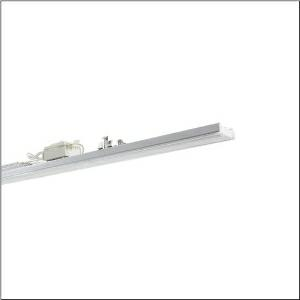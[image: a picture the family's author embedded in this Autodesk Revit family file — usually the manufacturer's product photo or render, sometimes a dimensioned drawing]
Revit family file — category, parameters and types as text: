
# Revit family: licross_21_recessed_ho_52tl18de47xm
name_source: partatom
category: Lighting Fixtures
units: mm (PartAtom-declared; Revit-internal decimal feet)

## family parameters
Cut with Voids When Loaded = No
Host = Face
Light Source = No
Part Type = Normal
Room Calculation Point = No
Round Connector Dimension = Use Diameter
Shared = No

## types (1)
- --- (1 x LED, 7420 lm, 44.1 W, 4000K)
    Apparent Load = 44 VA
    CIE Flux Codes = 75 94 99 100 100
    Color Rendering = 80
    Color Temperature = 4000K
    Default Elevation = 1800 mm
    Description = Licross 21 Recessed HO, luminaire insert, of sheet steel, galvanised, coil coated, white, length: 750mm, width: 66mm, height: 67mm, LED rated luminous flux: 7.420lm, light colour: 840, SDCM (Standard Deviation of Colour Matching)MacAdam ≤ 3 SDCM (initial), control gear: DALI 2, with plug, 5-pole, with phase selection, mains connection: 220..240V, AC, 50/60Hz, rated input power: 44W, internal wiring halogen-free, primary light control with lens, of plastic, primary optical cover: cover, of PMMA, light emission: direct distribution, primary light characteristic: symmetric, protection rating (complete): IP40, insulation class (complete): insulation class I (protective earthing), certification: CE, ENEC, VDE, UKCA, protection symbol: D if used in an environment without relevant dust loads with corresponding accessories, impact resistance: IK06, permissible ambient temperature for indoor applications: -25..+30°C, corresponds to IFS (International Featured Standards) requirements for safety and quality in the food industry, reducing of maximum allowable ambient temperature of 5°C with ceiling mounting, LABS conformity tested according to VDMA 24364:2018-05, The light source and the operating device comply with the requirements of the Ecodesign Regulation (EU) 2019/2020 and are replaceable in accordance with this regulation, packaging unit: 1 piece
    Height = 58 mm
    Lamp = 1 x LED
    Lamp Light Flux = 7420 lm
    Lamp Power = 44.1 W
    Lamp count = 1
    Length = 750 mm
    Luminous efficacy = 168 lm/W
    Manufacturer = Siteco
    ModVariant = No
    Model = 52TL18DE47XM
    Mounting Place = Ceiling
    Mounting Type = Pendant
    Number of Poles = 1
    OnlyDefault = Yes
    Power Factor = 1
    Product Name = Licross 21 Recessed HO
    Product group = luminaire insert | ceiling pendant
    ProductGroupID = 901
    Protection Class = Protection class I
    Protection Degree = IP 40
    RLX_Detail_Level = 1
    RLX_Emergency_Light_Flux = 0 lm
    RLX_Emergency_Type = 0
    RLX_Emergency_Type_DB = No
    RlxData = <blob elided: 29609 chars, md5=906f728f>
    Socket = socket
    Standby Power = 0 W
    System Light Flux = 7420 lm
    System Power = 44 W
    Type Comments = factory setting: luminous flux: 100 % | dim-lin: 254 | 484 mA
    Type Image = l_1296930.jpg
    URL = http://relux.com
    VarID = @adj_126045
    Voltage = 0 V
    Weight = 0.00 kg
    Width = 66 mm

## geometry (parser evidence)
native form markers: Blend x4, Sweep x9
no freeform markers — native parametric forms only
